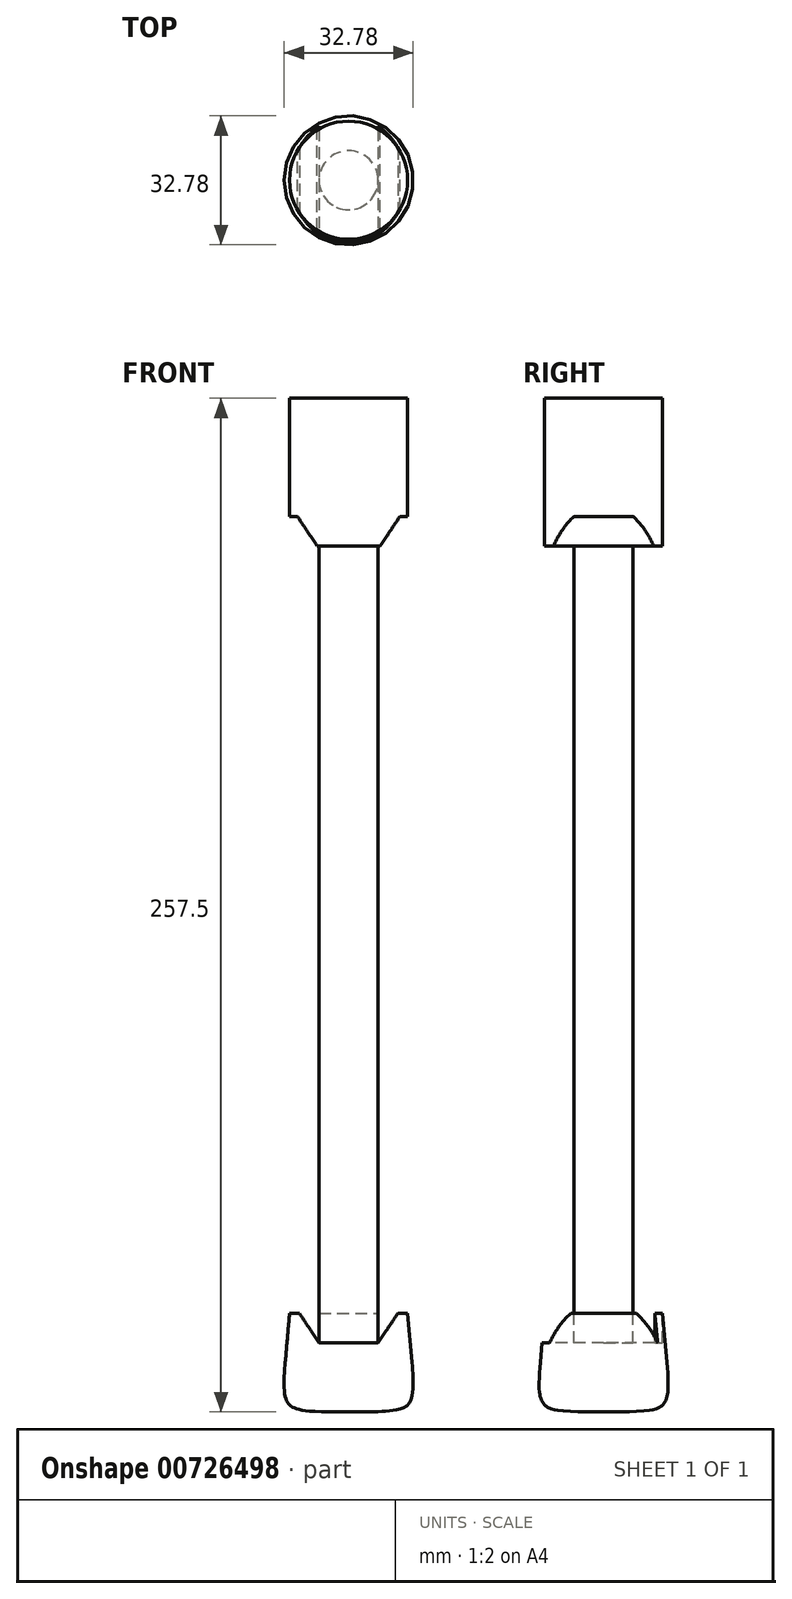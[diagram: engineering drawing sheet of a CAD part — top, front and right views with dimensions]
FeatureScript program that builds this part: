
annotation { "Feature Type Name" : "Feature", "Feature Type Description" : "" }
export const myFeature = defineFeature(function(context is Context, id is Id, definition is map)
    precondition{}
    {
        {
            var Q0;
            Q0=qCreatedBy(makeId("Top.planeOp"),FACE);
            var sketch = newSketch(context, id + "F0", { "sketchPlane" : qUnion([Q0])});
            skCircle(sketch, "E0", {"center": v(0, 0) * mm, "radius": 15 * mm});
            skSolve(sketch);
        }
        {
            var Q0;
            Q0 = qSketchRegion(id + "F0", true);
            extrude(context, id + "F1", {"entities" : qUnion([Q0]), "oppositeDirection" : true, "depth" : 30 * mm, "offsetDistance" : 25 * mm});
        }
        {
            var Q0;
            Q0=makeQuery(id+"F1.opExtrude","CAP_FACE",FACE,{"disambiguationData":[OSD([sQuery(id+"F0.wireOp",EDGE,"E0")])],"isStart":false});
            var sketch = newSketch(context, id + "F2", { "sketchPlane" : qUnion([Q0])});
            skCircle(sketch, "E1", {"center": v(0, 0) * mm, "radius": 7.5 * mm});
            skSolve(sketch);
        }
        {
            var Q0;
            Q0 = qSketchRegion(id + "F2", true);
            extrude(context, id + "F3", {"entities" : qUnion([Q0]), "operationType" : NewBodyOperationType.ADD, "depth" : 202.5 * mm, "offsetDistance" : 25 * mm});
        }
        {
            var Q0;
            Q0=makeQuery(id+"F3.opExtrude","CAP_FACE",FACE,{"disambiguationData":[OSD([sQuery(id+"F2.wireOp",EDGE,"E1")])],"isStart":false});
            var sketch = newSketch(context, id + "F4", { "sketchPlane" : qUnion([Q0])});
            skCircle(sketch, "E2", {"center": v(0, 0) * mm, "radius": 15 * mm});
            skSolve(sketch);
        }
        {
            var Q0;
            Q0 = qSketchRegion(id + "F4", true);
            extrude(context, id + "F5", {"entities" : qUnion([Q0]), "operationType" : NewBodyOperationType.ADD, "depth" : 25 * mm, "offsetDistance" : 25 * mm, "hasDraft" : true, "draftAngle" : 5 * degree});
        }
        {
            var Q0;
            Q0=qCreatedBy(makeId("Front.planeOp"),FACE);
            var sketch = newSketch(context, id + "F6", { "sketchPlane" : qUnion([Q0])});
            skLineSegment(sketch, "E3", {"start": v(-7.5, -232.5) * mm, "end": v(-7.5, -240) * mm});
            skLineSegment(sketch, "E4", {"start": v(-7.5, -240) * mm, "end": v(-12.5, -232.5) * mm});
            skLineSegment(sketch, "E5", {"start": v(-12.5, -232.5) * mm, "end": v(-7.5, -232.5) * mm});
            skLineSegment(sketch, "E6.MirrorCS", {"start": v(7.5, -232.5) * mm, "end": v(7.5, -240) * mm});
            skLineSegment(sketch, "E7.MirrorCS", {"start": v(7.5, -240) * mm, "end": v(12.5, -232.5) * mm});
            skLineSegment(sketch, "E8.MirrorCS", {"start": v(12.5, -232.5) * mm, "end": v(7.5, -232.5) * mm});
            skSolve(sketch);
        }
        {
            var Q0;
            Q0 = qSketchRegion(id + "F6", true);
            extrude(context, id + "F7", {"entities" : qUnion([Q0]), "operationType" : NewBodyOperationType.REMOVE, "endBound" : BoundingType.THROUGH_ALL, "oppositeDirection" : true, "depth" : 25 * mm, "offsetDistance" : 25 * mm, "hasSecondDirection" : true, "secondDirectionOppositeDirection" : false, "secondDirectionDepth" : 25 * mm});
        }
        {
            var Q0;
            {var subQ0=sQuery(id+"F4.wireOp",EDGE,"E2");var subQ1=makeQuery(id+"F5.opExtrude","CAP_FACE",FACE,{"disambiguationData":[OSD([subQ0])],"isStart":true});Q0=makeQuery(id+"F7.boolean.opBoolean","SPLIT",FACE,{"disambiguationData":[TD([makeQuery(id+"F3.opExtrude","SWEPT_FACE",FACE,{"disambiguationData":[OSD([sQuery(id+"F2.wireOp",EDGE,"E1")])]}),makeQuery(id+"F5.opExtrude","SWEPT_FACE",FACE,{"disambiguationData":[OSD([subQ0])]}),subQ1,makeQuery(id+"F7.opExtrude","SWEPT_FACE",FACE,{"disambiguationData":[OSD([sQuery(id+"F6.wireOp",EDGE,"E3")])]}),makeQuery(id+"F7.opExtrude","SWEPT_FACE",FACE,{"disambiguationData":[OSD([sQuery(id+"F6.wireOp",EDGE,"E6.MirrorCS")])]})]),OD(0.0)],"derivedFrom":subQ1});}
            var sketch = newSketch(context, id + "F8", { "sketchPlane" : qUnion([Q0])});
            skArc(sketch, "E9.0", {"start": v(7.5, -13) * mm, "mid": v(0, -15) * mm, "end": v(-7.5, -13) * mm});
            skLineSegment(sketch, "E10.0", {"start": v(-7.5, 0) * mm, "end": v(-7.5, -13) * mm});
            skArc(sketch, "E11.0", {"start": v(7.5, 0) * mm, "mid": v(0, -7.5) * mm, "end": v(-7.5, 0) * mm});
            skLineSegment(sketch, "E12.0", {"start": v(7.5, 0) * mm, "end": v(7.5, -13) * mm});
            skLineSegment(sketch, "E13.0", {"start": v(7.5, 13) * mm, "end": v(7.5, 0) * mm});
            skArc(sketch, "E14.0", {"start": v(-7.5, 13) * mm, "mid": v(0, 15) * mm, "end": v(7.5, 13) * mm});
            skLineSegment(sketch, "E15.0", {"start": v(-7.5, 13) * mm, "end": v(-7.5, 0) * mm});
            skArc(sketch, "E16.0", {"start": v(-7.5, 0) * mm, "mid": v(0, 7.5) * mm, "end": v(7.5, 0) * mm});
            skEllipticalArc(sketch, "E17.0", {});
            skEllipticalArc(sketch, "E18.0", {});
            skArc(sketch, "E19", {"start": v(7.5, 13.74) * mm, "mid": v(0, 15.66) * mm, "end": v(-7.5, 13.74) * mm});
            skLineSegment(sketch, "E20", {"start": v(-10.49, 0) * mm, "end": v(12.4, 0) * mm, "construction": true});
            skArc(sketch, "E21.MirrorCS", {"start": v(7.5, -13.74) * mm, "mid": v(0, -15.66) * mm, "end": v(-7.5, -13.74) * mm});
            skLineSegment(sketch, "E22", {"start": v(-7.5, 13) * mm, "end": v(-7.5, 13.74) * mm});
            skLineSegment(sketch, "E23", {"start": v(7.5, 13) * mm, "end": v(7.5, 13.74) * mm});
            skLineSegment(sketch, "E24", {"start": v(7.5, -13.74) * mm, "end": v(7.5, -13) * mm});
            skLineSegment(sketch, "E25", {"start": v(-7.5, -13.74) * mm, "end": v(-7.5, -13) * mm});
            const initialGuessF8  = {"E17.0": [0.0022220393492609625, 0, 1, 0, 0.016932017320564357, 0.016785581660288904, 2.1823995546250092, 2.6249436469543155], "E18.0": [-0.0022220393492609625, 0, -1, 0, 0.01693201732056436, 0.016785581660288908, 3.6582416602252685, 4.100785752554577]};
            skSetInitialGuess(sketch, initialGuessF8);
            skSolve(sketch);
        }
        {
            var Q0;
            Q0=makeQuery(id+"F8.imprint","IMPRINT",FACE,{"disambiguationData":[TD([[makeQuery(id+"F8.imprint","IMPRINT",EDGE,{"derivedFrom":sQuery(id+"F8.wireOp",EDGE,"E9.0")}),-1.0]])]});
            var Q1;
            Q1=makeQuery(id+"F8.imprint","IMPRINT",FACE,{"disambiguationData":[TD([[makeQuery(id+"F8.imprint","IMPRINT",EDGE,{"derivedFrom":sQuery(id+"F8.wireOp",EDGE,"E13.0")}),-1.0]])]});
            var Q2;
            Q2=makeQuery(id+"F8.imprint","IMPRINT",FACE,{"disambiguationData":[TD([[makeQuery(id+"F8.imprint","IMPRINT",EDGE,{"derivedFrom":sQuery(id+"F8.wireOp",EDGE,"E14.0")}),1.0]])]});
            var Q3;
            Q3=makeQuery(id+"F8.imprint","IMPRINT",FACE,{"disambiguationData":[TD([[makeQuery(id+"F8.imprint","IMPRINT",EDGE,{"derivedFrom":sQuery(id+"F8.wireOp",EDGE,"E9.0")}),1.0]])]});
            extrude(context, id + "F9", {"entities" : qUnion([Q0, Q1, Q2, Q3]), "operationType" : NewBodyOperationType.REMOVE, "oppositeDirection" : true, "depth" : 7.5 * mm, "offsetDistance" : 25 * mm});
        }
        {
            var Q0;
            Q0=qCreatedBy(makeId("Front.planeOp"),FACE);
            var sketch = newSketch(context, id + "F10", { "sketchPlane" : qUnion([Q0])});
            skLineSegment(sketch, "E26", {"start": v(-13.04, -30) * mm, "end": v(13.04, -30) * mm});
            skLineSegment(sketch, "E27", {"start": v(13.04, -30) * mm, "end": v(8.04, -37.5) * mm});
            skLineSegment(sketch, "E28", {"start": v(8.04, -37.5) * mm, "end": v(-8.04, -37.5) * mm});
            skLineSegment(sketch, "E29", {"start": v(-8.04, -37.5) * mm, "end": v(-13.04, -30) * mm});
            skSolve(sketch);
        }
        {
            var Q0;
            Q0=makeQuery(id+"F10.imprint","IMPRINT",FACE,{"disambiguationData":[TD([[makeQuery(id+"F10.imprint","IMPRINT",EDGE,{"derivedFrom":sQuery(id+"F10.wireOp",EDGE,"E26")}),-1.0]])]});
            var Q1;
            Q1=makeQuery(id+"F1.opExtrude","SWEPT_FACE",FACE,{"disambiguationData":[OSD([sQuery(id+"F0.wireOp",EDGE,"E0")])]});
            extrude(context, id + "F11", {"entities" : qUnion([Q0]), "operationType" : NewBodyOperationType.ADD, "endBound" : BoundingType.UP_TO_SURFACE, "depth" : 25 * mm, "endBoundEntityFace" : qUnion([Q1]), "offsetDistance" : 25 * mm});
        }
        {
            var Q0;
            Q0 = qSketchRegion(id + "F10", true);
            var Q1;
            {var subQ0=sQuery(id+"F0.wireOp",EDGE,"E0");Q1=makeQuery(id+"F11.boolean.opBoolean","MERGE",FACE,{"derivedFrom":[makeQuery(id+"F1.opExtrude","SWEPT_FACE",FACE,{"disambiguationData":[OSD([subQ0])]}),makeQuery(id+"F11.opExtrude","CAP_FACE",FACE,{"disambiguationData":[OSD([subQ0])],"isStart":false})]});}
            extrude(context, id + "F12", {"entities" : qUnion([Q0]), "operationType" : NewBodyOperationType.ADD, "endBound" : BoundingType.UP_TO_SURFACE, "oppositeDirection" : true, "depth" : 25 * mm, "endBoundEntityFace" : qUnion([Q1]), "offsetDistance" : 25 * mm});
        }
        {
            var Q0;
            Q0=makeQuery(id+"F5.opExtrude","CAP_FACE",FACE,{"disambiguationData":[OSD([sQuery(id+"F4.wireOp",EDGE,"E2")])],"isStart":false});
            fillet(context, id + "F13", {"entities" : qUnion([Q0]), "tangentPropagation" : true, "crossSection" : FilletCrossSection.CONIC, "radius" : 11.5 * mm, "rho" : 0.7, "defaultsChanged" : true, "vertexSettings" : [], "allowEdgeOverflow" : false});
        }
    });
